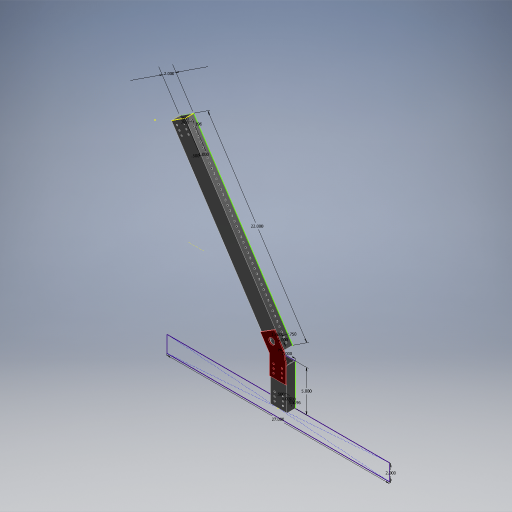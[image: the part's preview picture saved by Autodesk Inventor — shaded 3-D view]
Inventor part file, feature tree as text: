
AUTODESK INVENTOR PART (.ipt)
format: ipt  version: 2024.2 (Build 282272000, 272)  size: 582,656 bytes
history: native  units: in
note: dims shown in document units (in); Inventor stores cm internally (conversion verified against a paired STEP export)
features: sketch x6, extrude x6, projected_geometry x5, other x3
ambient origin geometry x8: Origin, YZ Plane, XZ Plane, XY Plane, X Axis, Y Axis, Z Axis, Center Point
bodies: Body1 (feature_tree), Body2 (feature_tree), Body3 (feature_tree)
feature tree (20):
  other  "Shootaur-Structure"
  sketch  "Sketch1"  dims[d0=27.0in d1=2.0in]
  extrude  "Extrusion8"  Depth=2.0in
  extrude  "Extrusion9"  Depth=5.0in
  extrude  "Extrusion10"  Depth=0.5in
  extrude  "Extrusion11"  Depth=2.0in
  sketch  "Sketch9"  dims[d24=0.7874in d26=1.0in d27=1.1811in d29=0.5in d60=2.0in]
  extrude  "Extrusion12"  Depth=2.0in
  extrude  "Extrusion13"  Depth=1.0in
  other  "Back-Support"
  sketch  "Sketch7"  dims[d5=5.0in d21=0.196in]
  projected_geometry  "Projected Loop5"
  projected_geometry  "Projected Loop6"
  other  "Dead-Axle-Gusset"
  sketch  "Sketch8"  dims[d22=0.5in d23=0.5in]
  projected_geometry  "Projected Loop7"
  projected_geometry  "Projected Loop8"
  sketch  "Sketch10"  dims[d61=2.0in d62=0.196in]
  projected_geometry  "Projected Loop9"
  sketch  "Sketch11"  dims[d63=0.5in d64=0.5in d65=0.7874in d67=1.0in d68=1.1811in d70=0.5in d73=0.75in d74=1.0in d75=1.0in d76=1.0in d77=0.0in d78=1.0in d79=0.0in d80=2.0in d81=2.0in d82=0.125in d83=0.0in d84=0.0625in d85=8.25in d86=0.0in d87=22.0in d88=0.0625in d89=1.0in d90=0.0in d91=0.196in d92=0.5in d93=0.5in d94=16.9291in d96=0.5in d97=0.3937in d99=1.0in d101=4.952in d102=0.0in d46=0.5in d47=0.0344in d48=0.5in d49=0.0344in d50=0.5in d51=0.0344in d52=0.5in d53=0.0344in d54=0.5in d55=0.0344in]
